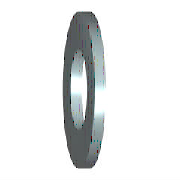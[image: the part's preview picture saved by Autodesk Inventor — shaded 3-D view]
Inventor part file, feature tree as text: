
AUTODESK INVENTOR PART (.ipt)
format: ipt  version: 2019 (Build 230136000, 136)  size: 108,544 bytes
history: native  units: mm (DEFAULTED — no unit token found)
features: other x1, plane x1, sketch x1
ambient origin geometry x7: Origin, YZ Plane, XY Plane, X Axis, Y Axis, Z Axis, Center Point
bodies: Solid1 (feature_tree), Body (feature_tree)
feature tree (3):
  other  "Work Axis1"
  plane  "Work Plane1"
  sketch  "Sketch"  dims[d0=4.3mm d1=9.0mm d2=0.8mm d3=0.0mm d4=0.0mm d5=0.0mm d6=0.0mm d7=0.0mm]
